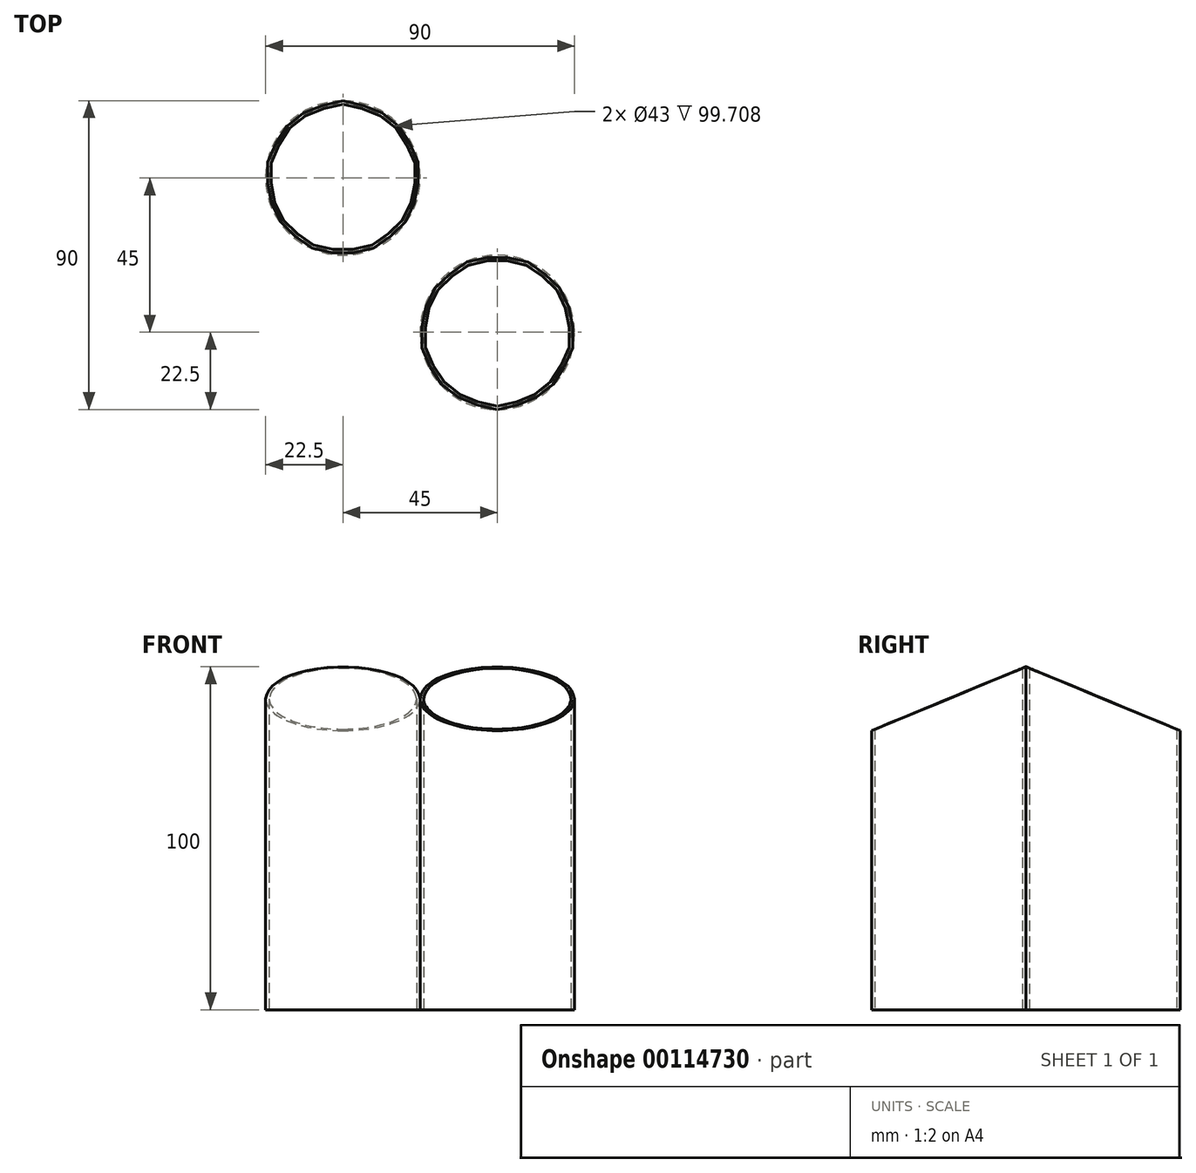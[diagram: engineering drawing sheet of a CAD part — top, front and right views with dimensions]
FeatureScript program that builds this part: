
annotation { "Feature Type Name" : "Feature", "Feature Type Description" : "" }
export const myFeature = defineFeature(function(context is Context, id is Id, definition is map)
    precondition{}
    {
        {
            var Q0;
            Q0=qCreatedBy(makeId("Top.planeOp"),FACE);
            var sketch = newSketch(context, id + "F0", { "sketchPlane" : qUnion([Q0])});
            skCircle(sketch, "E0", {"center": v(-22.5, 22.5) * mm, "radius": 21.5 * mm});
            skCircle(sketch, "E1", {"center": v(-22.5, 22.5) * mm, "radius": 22.5 * mm});
            skSolve(sketch);
        }
        {
            var Q0;
            Q0=makeQuery(id+"F0.imprint","IMPRINT",FACE,{"disambiguationData":[TD([[makeQuery(id+"F0.imprint","IMPRINT",EDGE,{"derivedFrom":sQuery(id+"F0.wireOp",EDGE,"E0")}),-1.0]])]});
            extrude(context, id + "F1", {"entities" : qUnion([Q0]), "depth" : 100 * mm});
        }
        {
            var Q0;
            Q0=qCreatedBy(makeId("Right.planeOp"),FACE);
            var sketch = newSketch(context, id + "F2", { "sketchPlane" : qUnion([Q0])});
            skLineSegment(sketch, "E2", {"start": v(0, 100) * mm, "end": v(48.67, 79.84) * mm});
            skLineSegment(sketch, "E3", {"start": v(0, 100) * mm, "end": v(0, 114.38) * mm});
            skLineSegment(sketch, "E4", {"start": v(0, 114.38) * mm, "end": v(48.67, 114.38) * mm});
            skLineSegment(sketch, "E5", {"start": v(48.67, 114.38) * mm, "end": v(48.67, 79.84) * mm});
            skSolve(sketch);
        }
        {
            var Q0;
            Q0=makeQuery(id+"F2.imprint","IMPRINT",FACE,{"disambiguationData":[TD([[makeQuery(id+"F2.imprint","IMPRINT",EDGE,{"derivedFrom":sQuery(id+"F2.wireOp",EDGE,"E2")}),1.0]])]});
            extrude(context, id + "F3", {"entities" : qUnion([Q0]), "operationType" : NewBodyOperationType.REMOVE, "oppositeDirection" : true, "depth" : 100 * mm});
        }
        {
            var Q0;
            Q0=qCreatedBy(makeId("Top.planeOp"),FACE);
            var sketch = newSketch(context, id + "F4", { "sketchPlane" : qUnion([Q0])});
            skCircle(sketch, "E6", {"center": v(22.5, -22.5) * mm, "radius": 21.5 * mm});
            skCircle(sketch, "E7", {"center": v(22.5, -22.5) * mm, "radius": 22.5 * mm});
            skSolve(sketch);
        }
        {
            var Q0;
            Q0 = qSketchRegion(id + "F4", true);
            extrude(context, id + "F5", {"entities" : qUnion([Q0]), "depth" : 100 * mm});
        }
        {
            var Q0;
            Q0=qCreatedBy(makeId("Right.planeOp"),FACE);
            var sketch = newSketch(context, id + "F6", { "sketchPlane" : qUnion([Q0])});
            skLineSegment(sketch, "E8", {"start": v(0, 100) * mm, "end": v(-57.52, 76.17) * mm});
            skLineSegment(sketch, "E9", {"start": v(0, 100) * mm, "end": v(0, 116.92) * mm});
            skLineSegment(sketch, "E10", {"start": v(0, 116.92) * mm, "end": v(-57.52, 116.92) * mm});
            skLineSegment(sketch, "E11", {"start": v(-57.52, 116.92) * mm, "end": v(-57.52, 76.17) * mm});
            skSolve(sketch);
        }
        {
            var Q0;
            Q0=makeQuery(id+"F6.imprint","IMPRINT",FACE,{"disambiguationData":[TD([[makeQuery(id+"F6.imprint","IMPRINT",EDGE,{"derivedFrom":sQuery(id+"F6.wireOp",EDGE,"E8")}),-1.0]])]});
            extrude(context, id + "F7", {"entities" : qUnion([Q0]), "operationType" : NewBodyOperationType.REMOVE, "depth" : 100 * mm});
        }
    });
